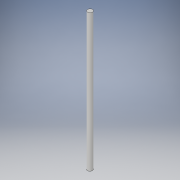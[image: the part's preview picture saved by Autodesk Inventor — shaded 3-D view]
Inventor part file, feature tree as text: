
AUTODESK INVENTOR PART (.ipt)
format: ipt  version: 2019 (Build 230136000, 136)  size: 90,112 bytes
history: native  units: mm
features: extrude x1, sketch x1
ambient origin geometry x8: Origin, YZ Plane, XZ Plane, XY Plane, X Axis, Y Axis, Z Axis, Center Point
bodies: Solid1 (feature_tree)
feature tree (2):
  extrude  "Extrusion1"  Depth=140.0mm TaperAngle=0.0deg
  sketch  "Sketch1"  dims[d0=5.0mm d1=140.0mm d2=0.0mm]
